# Revit family: Gorter-U_0600-0600
name_source: partatom
category: Generic Models
revit_build: Autodesk Revit 2017 (Build: 20171027_0315(x64)
units: mm (PartAtom-declared; Revit-internal decimal feet)

## family parameters
Always vertical = Yes
Can host rebar = No
Cut with Voids When Loaded = No
Host = Wall
Part Type = Normal
Room Calculation Point = No
Round Connector Dimension = Use Diameter
Shared = Yes

## types (6) — shared parameters
Bevestiging = voorgeboorde bevestigingsgaten
Model = Wandluik universeel
URL = https://www.gortergroup.com
afstand tot wand = 2 mm  [stored 0.00656168 ft]
draairichting aanzicht = Yes
draairichting plattegrond = Yes
frame = KTL behandeld staal - RAL9010
wandluik = KTL behandeld staal - RAL9010

## per-type parameters (varying)
| type | A | B | Sparingsmaat A | Sparingsmaat B | Weight (kg) |
| U-0250-0250 | 250 mm  [stored 0.82021 ft] | 250 mm  [stored 0.82021 ft] | 277 mm  [stored 0.908793 ft] | 277 mm  [stored 0.908793 ft] | 2 |
| U-0400-0400 | 400 mm  [stored 1.31234 ft] | 400 mm  [stored 1.31234 ft] | 427 mm | 427 mm | 4 |
| U-0500-0500 | 500 mm  [stored 1.64042 ft] | 500 mm  [stored 1.64042 ft] | 527 mm | 527 mm | 6 |
| U-0600-0600 | 600 mm | 600 mm | 627 mm  [stored 2.05709 ft] | 627 mm  [stored 2.05709 ft] | 8 |
| U-0600-0800 | 600 mm | 800 mm  [stored 2.62467 ft] | 627 mm  [stored 2.05709 ft] | 827 mm  [stored 2.71325 ft] | 10 |
| U-0800-0800 | 800 mm  [stored 2.62467 ft] | 800 mm  [stored 2.62467 ft] | 827 mm  [stored 2.71325 ft] | 827 mm  [stored 2.71325 ft] | 12 |

note: [stored X ft] marks values corroborated as IEEE doubles in the binary element streams (Revit-internal decimal feet)

## geometry (parser evidence)
native form markers: Sweep x4
no freeform markers — native parametric forms only
